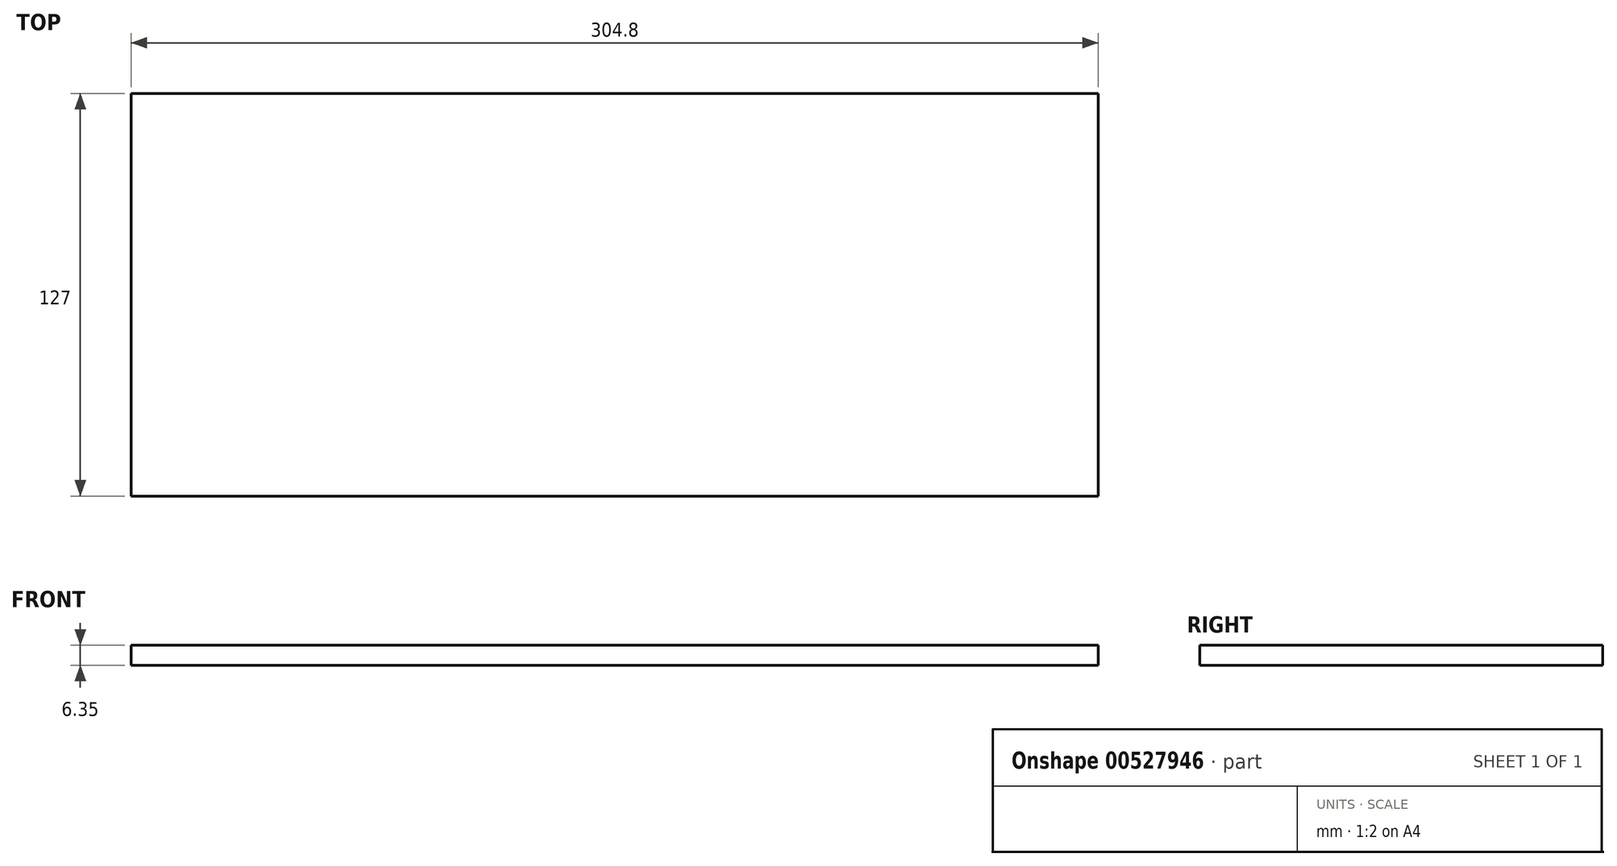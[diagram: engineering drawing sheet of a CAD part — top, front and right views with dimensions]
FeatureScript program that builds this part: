
annotation { "Feature Type Name" : "Feature", "Feature Type Description" : "" }
export const myFeature = defineFeature(function(context is Context, id is Id, definition is map)
    precondition{}
    {
        {
            var Q0;
            Q0=qCreatedBy(makeId("Top.planeOp"),FACE);
            var sketch = newSketch(context, id + "F0", { "sketchPlane" : qUnion([Q0])});
            skLineSegment(sketch, "E0.bottom", {"start": v(-152.4, 63.5) * mm, "end": v(152.4, 63.5) * mm});
            skLineSegment(sketch, "E0.top", {"start": v(-152.4, -63.5) * mm, "end": v(152.4, -63.5) * mm});
            skLineSegment(sketch, "E0.left", {"start": v(-152.4, 63.5) * mm, "end": v(-152.4, -63.5) * mm});
            skLineSegment(sketch, "E0.right", {"start": v(152.4, 63.5) * mm, "end": v(152.4, -63.5) * mm});
            skPoint(sketch, "E0.middle", {"position": v(0, 0) * mm});
            skSolve(sketch);
        }
        {
            var Q0;
            Q0 = qSketchRegion(id + "F0", true);
            extrude(context, id + "F1", {"entities" : qUnion([Q0]), "depth" : 6.35 * mm, "offsetDistance" : 25.4 * mm});
        }
    });
